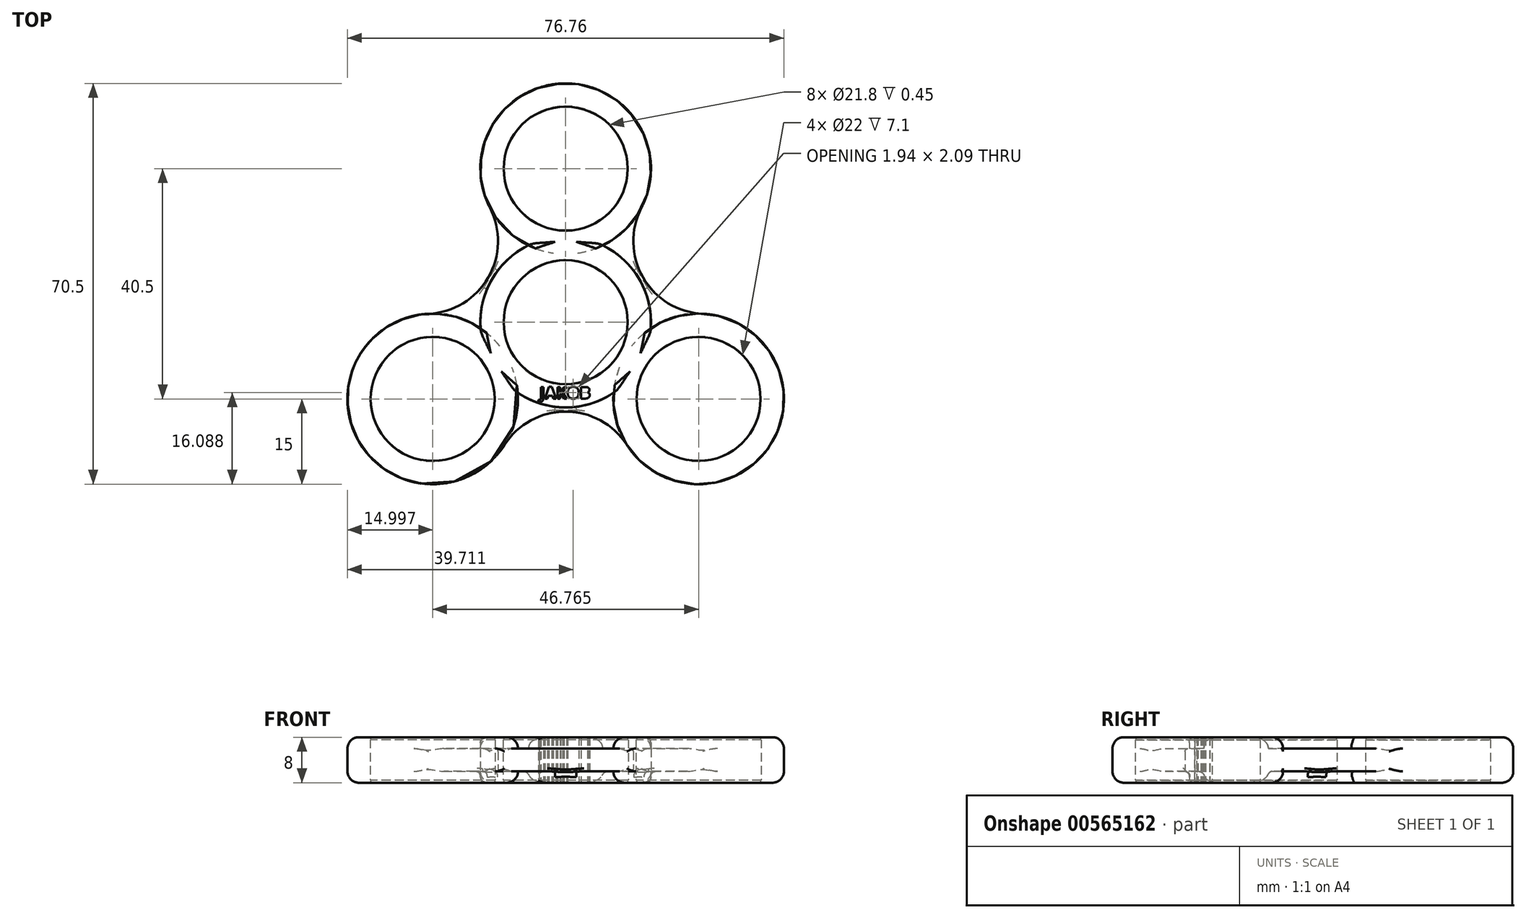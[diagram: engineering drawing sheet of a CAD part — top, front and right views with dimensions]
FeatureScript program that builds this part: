
annotation { "Feature Type Name" : "Feature", "Feature Type Description" : "" }
export const myFeature = defineFeature(function(context is Context, id is Id, definition is map)
    precondition{}
    {
        {
            var Q0;
            Q0=qCreatedBy(makeId("Top.planeOp"),FACE);
            var sketch = newSketch(context, id + "F0", { "sketchPlane" : qUnion([Q0])});
            skCircle(sketch, "E0", {"center": v(0, 0) * mm, "radius": 10.9 * mm});
            skCircle(sketch, "E1", {"center": v(0, 27) * mm, "radius": 10.9 * mm});
            skCircle(sketch, "E2.1.0", {"center": v(-23.38, -13.5) * mm, "radius": 10.9 * mm});
            skCircle(sketch, "E2.2.0", {"center": v(23.38, -13.5) * mm, "radius": 10.9 * mm});
            skArc(sketch, "E3", {"start": v(6.54, 13.5) * mm, "mid": v(0, 42) * mm, "end": v(-6.54, 13.5) * mm});
            skArc(sketch, "E4.1.0", {"start": v(8.42, -12.41) * mm, "mid": v(36.37, -21) * mm, "end": v(14.96, -1.09) * mm});
            skArc(sketch, "E4.2.0", {"start": v(-14.96, -1.09) * mm, "mid": v(-36.37, -21) * mm, "end": v(-8.42, -12.41) * mm});
            skArc(sketch, "E5", {"start": v(-8.42, -12.41) * mm, "mid": v(0, -15) * mm, "end": v(8.42, -12.41) * mm});
            skArc(sketch, "E6", {"start": v(-24.08, 1.48) * mm, "mid": v(-13.61, 7.86) * mm, "end": v(-13.33, 20.12) * mm});
            skArc(sketch, "E7", {"start": v(10.76, -21.6) * mm, "mid": v(0, -15.72) * mm, "end": v(-10.76, -21.6) * mm});
            skArc(sketch, "E8", {"start": v(13.33, 20.12) * mm, "mid": v(13.61, 7.86) * mm, "end": v(24.08, 1.48) * mm});
            skPoint(sketch, "E9.orphan", {"position": v(-13, 34.5) * mm});
            skPoint(sketch, "E10.orphan", {"position": v(-36.37, -6) * mm});
            skPoint(sketch, "E11.orphan", {"position": v(13, 34.5) * mm});
            skPoint(sketch, "E12.2.0.start.orphan", {"position": v(36.37, -6) * mm});
            skPoint(sketch, "E13.orphan", {"position": v(23.38, -28.5) * mm});
            skPoint(sketch, "E12.1.0.start.orphan", {"position": v(-23.38, -28.5) * mm});
            skArc(sketch, "E14.trimOffspring", {"start": v(14.96, -1.09) * mm, "mid": v(13, 7.5) * mm, "end": v(6.54, 13.5) * mm});
            skArc(sketch, "E15.trimOffspring", {"start": v(-6.54, 13.5) * mm, "mid": v(-13, 7.5) * mm, "end": v(-14.96, -1.09) * mm});
            skText(sketch, "E16", { "text": "JAKOB", "fontName": "OpenSans-Bold.ttf"});
            skCircle(sketch, "E17", {"center": v(23.38, -13.5) * mm, "radius": 11 * mm});
            skCircle(sketch, "E18", {"center": v(-23.38, -13.5) * mm, "radius": 11 * mm});
            skCircle(sketch, "E19", {"center": v(0, 0) * mm, "radius": 11 * mm});
            skCircle(sketch, "E20", {"center": v(0, 27) * mm, "radius": 11 * mm});
            const initialGuessF0  = {"E16": [-0.0046, -0.01343, 1, 0, 0.00205]};
            skSetInitialGuess(sketch, initialGuessF0);
            skSolve(sketch);
        }
        {
            var Q0;
            Q0=makeQuery(id+"F0.imprint","IMPRINT",FACE,{"disambiguationData":[TD([[makeQuery(id+"F0.imprint","IMPRINT",EDGE,{"derivedFrom":sQuery(id+"F0.wireOp",EDGE,"E2.1.0")}),-1.0]])]});
            var Q1;
            Q1=makeQuery(id+"F0.imprint","IMPRINT",FACE,{"disambiguationData":[TD([[makeQuery(id+"F0.imprint","IMPRINT",EDGE,{"derivedFrom":sQuery(id+"F0.wireOp",EDGE,"E0")}),-1.0]])]});
            var Q2;
            Q2=makeQuery(id+"F0.imprint","IMPRINT",FACE,{"disambiguationData":[TD([[makeQuery(id+"F0.imprint","IMPRINT",EDGE,{"derivedFrom":sQuery(id+"F0.wireOp",EDGE,"E1")}),-1.0]])]});
            var Q3;
            {var subQ0=sQuery(id+"F0.wireOp",EDGE,"E3");var subQ1=sQuery(id+"F0.wireOp",EDGE,"KJlQqC9l-gusD-toYh-YzLE-zyJcLNbmcpUm");var subQ2=makeQuery(id+"F0.imprint","INTERSECT",VERTEX,{"derivedFrom":[subQ1,subQ0]});Q3=makeQuery(id+"F0.imprint","IMPRINT",FACE,{"disambiguationData":[TD([[makeQuery(id+"F0.imprint","IMPRINT",EDGE,{"disambiguationData":[TD([[subQ2,1.0]])],"derivedFrom":subQ1}),1.0]])]});}
            var Q4;
            {var subQ0=sQuery(id+"F0.wireOp",EDGE,"E3");var subQ1=sQuery(id+"F0.wireOp",EDGE,"KJlQqC9l-gusD-toYh-YzLE-zyJcLNbmcpUm");var subQ2=makeQuery(id+"F0.imprint","INTERSECT",VERTEX,{"derivedFrom":[subQ1,subQ0]});Q4=makeQuery(id+"F0.imprint","IMPRINT",FACE,{"disambiguationData":[TD([[makeQuery(id+"F0.imprint","IMPRINT",EDGE,{"disambiguationData":[TD([[subQ2,1.0]])],"derivedFrom":subQ1}),-1.0]])]});}
            var Q5;
            {var subQ0=sQuery(id+"F0.wireOp",EDGE,"E5");var subQ1=sQuery(id+"F0.wireOp",EDGE,"E4.2.0");var subQ2=makeQuery(id+"F0.imprint","INTERSECT",VERTEX,{"disambiguationData":[OD(0.0)],"derivedFrom":[subQ1,subQ0]});Q5=makeQuery(id+"F0.imprint","IMPRINT",FACE,{"disambiguationData":[TD([[makeQuery(id+"F0.imprint","IMPRINT",EDGE,{"disambiguationData":[TD([[subQ2,-1.0]])],"derivedFrom":subQ1}),1.0]])]});}
            var Q6;
            Q6=makeQuery(id+"F0.imprint","IMPRINT",FACE,{"disambiguationData":[TD([[makeQuery(id+"F0.imprint","IMPRINT",EDGE,{"derivedFrom":sQuery(id+"F0.wireOp",EDGE,"E2.2.0")}),-1.0]])]});
            var Q7;
            {var subQ0=sQuery(id+"F0.wireOp",EDGE,"E5");var subQ1=sQuery(id+"F0.wireOp",EDGE,"E4.1.0");var subQ2=makeQuery(id+"F0.imprint","INTERSECT",VERTEX,{"disambiguationData":[OD(0.0)],"derivedFrom":[subQ1,subQ0]});Q7=makeQuery(id+"F0.imprint","IMPRINT",FACE,{"disambiguationData":[TD([[makeQuery(id+"F0.imprint","IMPRINT",EDGE,{"disambiguationData":[TD([[subQ2,-1.0]])],"derivedFrom":subQ1}),1.0]])]});}
            extrude(context, id + "F1", {"entities" : qUnion([Q0, Q1, Q2, Q3, Q4, Q5, Q6, Q7]), "endBound" : BoundingType.SYMMETRIC, "depth" : 8 * mm, "offsetDistance" : 25 * mm});
        }
        {
            var Q0;
            {var subQ0=sQuery(id+"F0.wireOp",EDGE,"E7");Q0=makeQuery(id+"F0.imprint","IMPRINT",FACE,{"disambiguationData":[TD([[makeQuery(id+"F0.imprint","IMPRINT",EDGE,{"derivedFrom":subQ0}),-1.0]])]});}
            var Q1;
            {var subQ0=sQuery(id+"F0.wireOp",EDGE,"E6");Q1=makeQuery(id+"F0.imprint","IMPRINT",FACE,{"disambiguationData":[TD([[makeQuery(id+"F0.imprint","IMPRINT",EDGE,{"derivedFrom":subQ0}),-1.0]])]});}
            var Q2;
            {var subQ0=sQuery(id+"F0.wireOp",EDGE,"E8");Q2=makeQuery(id+"F0.imprint","IMPRINT",FACE,{"disambiguationData":[TD([[makeQuery(id+"F0.imprint","IMPRINT",EDGE,{"derivedFrom":subQ0}),-1.0]])]});}
            extrude(context, id + "F2", {"entities" : qUnion([Q0, Q1, Q2]), "operationType" : NewBodyOperationType.ADD, "endBound" : BoundingType.SYMMETRIC, "depth" : 4 * mm, "offsetDistance" : 25 * mm});
        }
        {
            var Q0;
            Q0=makeQuery(id+"F1.opExtrude","CAP_EDGE",EDGE,{"disambiguationData":[OSD([sQuery(id+"F0.wireOp",EDGE,"E15.trimOffspring")])],"isStart":true});
            var Q1;
            Q1=makeQuery(id+"F2.opExtrude","CAP_EDGE",EDGE,{"disambiguationData":[OSD([sQuery(id+"F0.wireOp",EDGE,"E15.trimOffspring")])],"isStart":true});
            var Q2;
            Q2=makeQuery(id+"F1.opExtrude","CAP_EDGE",EDGE,{"disambiguationData":[OSD([sQuery(id+"F0.wireOp",EDGE,"E5")])],"isStart":true});
            var Q3;
            Q3=makeQuery(id+"F2.opExtrude","CAP_EDGE",EDGE,{"disambiguationData":[OSD([sQuery(id+"F0.wireOp",EDGE,"E5")])],"isStart":true});
            var Q4;
            Q4=makeQuery(id+"F1.opExtrude","CAP_EDGE",EDGE,{"disambiguationData":[OSD([sQuery(id+"F0.wireOp",EDGE,"E14.trimOffspring")])],"isStart":true});
            var Q5;
            Q5=makeQuery(id+"F2.opExtrude","CAP_EDGE",EDGE,{"disambiguationData":[OSD([sQuery(id+"F0.wireOp",EDGE,"E14.trimOffspring")])],"isStart":true});
            fillet(context, id + "F3", {"entities" : qUnion([Q0, Q1, Q2, Q3, Q4, Q5]), "radius" : 1 * mm, "rho" : 0.5, "crossSection" : FilletCrossSection.CONIC, "allowEdgeOverflow" : false});
        }
        {
            var Q0;
            Q0=makeQuery(id+"F1.opExtrude","CAP_EDGE",EDGE,{"disambiguationData":[OSD([sQuery(id+"F0.wireOp",EDGE,"E5")])],"isStart":false});
            var Q1;
            Q1=makeQuery(id+"F2.opExtrude","CAP_EDGE",EDGE,{"disambiguationData":[OSD([sQuery(id+"F0.wireOp",EDGE,"E5")])],"isStart":false});
            var Q2;
            Q2=makeQuery(id+"F1.opExtrude","CAP_EDGE",EDGE,{"disambiguationData":[OSD([sQuery(id+"F0.wireOp",EDGE,"E14.trimOffspring")])],"isStart":false});
            var Q3;
            Q3=makeQuery(id+"F2.opExtrude","CAP_EDGE",EDGE,{"disambiguationData":[OSD([sQuery(id+"F0.wireOp",EDGE,"E14.trimOffspring")])],"isStart":false});
            var Q4;
            Q4=makeQuery(id+"F1.opExtrude","CAP_EDGE",EDGE,{"disambiguationData":[OSD([sQuery(id+"F0.wireOp",EDGE,"E15.trimOffspring")])],"isStart":false});
            var Q5;
            Q5=makeQuery(id+"F2.opExtrude","CAP_EDGE",EDGE,{"disambiguationData":[OSD([sQuery(id+"F0.wireOp",EDGE,"E15.trimOffspring")])],"isStart":false});
            fillet(context, id + "F4", {"entities" : qUnion([Q0, Q1, Q2, Q3, Q4, Q5]), "radius" : 1 * mm, "rho" : 0.5, "crossSection" : FilletCrossSection.CONIC, "allowEdgeOverflow" : false});
        }
        {
            var Q0;
            Q0=makeQuery(id+"F1.opExtrude","CAP_EDGE",EDGE,{"disambiguationData":[OSD([sQuery(id+"F0.wireOp",EDGE,"E4.1.0")])],"isStart":false});
            var Q1;
            Q1=makeQuery(id+"F1.opExtrude","CAP_EDGE",EDGE,{"disambiguationData":[OSD([sQuery(id+"F0.wireOp",EDGE,"E3")])],"isStart":false});
            var Q2;
            Q2=makeQuery(id+"F1.opExtrude","CAP_EDGE",EDGE,{"disambiguationData":[OSD([sQuery(id+"F0.wireOp",EDGE,"E4.2.0")])],"isStart":false});
            var Q3;
            Q3=makeQuery(id+"F1.opExtrude","CAP_EDGE",EDGE,{"disambiguationData":[OSD([sQuery(id+"F0.wireOp",EDGE,"E4.2.0")])],"isStart":true});
            var Q4;
            Q4=makeQuery(id+"F1.opExtrude","CAP_EDGE",EDGE,{"disambiguationData":[OSD([sQuery(id+"F0.wireOp",EDGE,"E4.1.0")])],"isStart":true});
            var Q5;
            Q5=makeQuery(id+"F1.opExtrude","CAP_EDGE",EDGE,{"disambiguationData":[OSD([sQuery(id+"F0.wireOp",EDGE,"E3")])],"isStart":true});
            fillet(context, id + "F5", {"entities" : qUnion([Q0, Q1, Q2, Q3, Q4, Q5]), "radius" : 2 * mm, "allowEdgeOverflow" : false});
        }
        {
            var Q0;
            Q0=makeQuery(id+"F2.opExtrude","SWEPT_FACE",FACE,{"disambiguationData":[OSD([sQuery(id+"F0.wireOp",EDGE,"E8")])]});
            var Q1;
            Q1=makeQuery(id+"F2.opExtrude","SWEPT_FACE",FACE,{"disambiguationData":[OSD([sQuery(id+"F0.wireOp",EDGE,"E6")])]});
            var Q2;
            Q2=makeQuery(id+"F2.opExtrude","SWEPT_FACE",FACE,{"disambiguationData":[OSD([sQuery(id+"F0.wireOp",EDGE,"E7")])]});
            fillet(context, id + "F6", {"entities" : qUnion([Q0, Q1, Q2]), "radius" : .5 * mm, "tangentPropagation" : true, "allowEdgeOverflow" : false});
        }
        {
            var Q0;
            Q0=makeQuery(id+"F0.imprint","IMPRINT",FACE,{"disambiguationData":[TD([[makeQuery(id+"F0.imprint","IMPRINT",EDGE,{"derivedFrom":sQuery(id+"F0.wireOp",EDGE,"E20")}),1.0]])]});
            var Q1;
            Q1=makeQuery(id+"F0.imprint","IMPRINT",FACE,{"disambiguationData":[TD([[makeQuery(id+"F0.imprint","IMPRINT",EDGE,{"derivedFrom":sQuery(id+"F0.wireOp",EDGE,"E19")}),1.0]])]});
            var Q2;
            Q2=makeQuery(id+"F0.imprint","IMPRINT",FACE,{"disambiguationData":[TD([[makeQuery(id+"F0.imprint","IMPRINT",EDGE,{"derivedFrom":sQuery(id+"F0.wireOp",EDGE,"E17")}),1.0]])]});
            var Q3;
            Q3=makeQuery(id+"F0.imprint","IMPRINT",FACE,{"disambiguationData":[TD([[makeQuery(id+"F0.imprint","IMPRINT",EDGE,{"derivedFrom":sQuery(id+"F0.wireOp",EDGE,"E18")}),1.0]])]});
            extrude(context, id + "F7", {"entities" : qUnion([Q0, Q1, Q2, Q3]), "endBound" : BoundingType.SYMMETRIC, "depth" : 7.1 * mm, "offsetDistance" : 25 * mm});
        }
        {
            var Q0;
            Q0=makeQuery(id+"F7.opExtrude","SWEPT_BODY",BODY,{"disambiguationData":[OSD([sQuery(id+"F0.wireOp",EDGE,"E17")])]});
            var Q1;
            Q1=makeQuery(id+"F7.opExtrude","SWEPT_BODY",BODY,{"disambiguationData":[OSD([sQuery(id+"F0.wireOp",EDGE,"E18")])]});
            var Q2;
            Q2=makeQuery(id+"F7.opExtrude","SWEPT_BODY",BODY,{"disambiguationData":[OSD([sQuery(id+"F0.wireOp",EDGE,"E19")])]});
            var Q3;
            Q3=makeQuery(id+"F7.opExtrude","SWEPT_BODY",BODY,{"disambiguationData":[OSD([sQuery(id+"F0.wireOp",EDGE,"E20")])]});
            var Q4;
            Q4=makeQuery(id+"F1.opExtrude","SWEPT_BODY",BODY,{"disambiguationData":[OSD([sQuery(id+"F0.wireOp",EDGE,"E0"),sQuery(id+"F0.wireOp",EDGE,"E1"),sQuery(id+"F0.wireOp",EDGE,"E2.1.0"),sQuery(id+"F0.wireOp",EDGE,"E2.2.0"),sQuery(id+"F0.wireOp",EDGE,"E3"),sQuery(id+"F0.wireOp",EDGE,"E4.1.0"),sQuery(id+"F0.wireOp",EDGE,"E4.2.0"),sQuery(id+"F0.wireOp",EDGE,"E5"),sQuery(id+"F0.wireOp",EDGE,"E14.trimOffspring"),sQuery(id+"F0.wireOp",EDGE,"E15.trimOffspring"),sQuery(id+"F0.wireOp",EDGE,"E16.sketch_text.stroke-7"),sQuery(id+"F0.wireOp",EDGE,"E16.sketch_text.stroke-8"),sQuery(id+"F0.wireOp",EDGE,"E16.sketch_text.stroke-9"),sQuery(id+"F0.wireOp",EDGE,"E16.sketch_text.stroke-10"),sQuery(id+"F0.wireOp",EDGE,"E16.sketch_text.stroke-11"),sQuery(id+"F0.wireOp",EDGE,"E16.sketch_text.stroke-12"),sQuery(id+"F0.wireOp",EDGE,"E16.sketch_text.stroke-13"),sQuery(id+"F0.wireOp",EDGE,"E16.sketch_text.stroke-14"),sQuery(id+"F0.wireOp",EDGE,"E16.sketch_text.stroke-15"),sQuery(id+"F0.wireOp",EDGE,"E16.sketch_text.stroke-16"),sQuery(id+"F0.wireOp",EDGE,"E16.sketch_text.stroke-17"),sQuery(id+"F0.wireOp",EDGE,"E16.sketch_text.stroke-18"),sQuery(id+"F0.wireOp",EDGE,"E16.sketch_text.stroke-19"),sQuery(id+"F0.wireOp",EDGE,"E16.sketch_text.stroke-20"),sQuery(id+"F0.wireOp",EDGE,"E16.sketch_text.stroke-21"),sQuery(id+"F0.wireOp",EDGE,"E16.sketch_text.stroke-22"),sQuery(id+"F0.wireOp",EDGE,"E16.sketch_text.stroke-23"),sQuery(id+"F0.wireOp",EDGE,"E16.sketch_text.stroke-28"),sQuery(id+"F0.wireOp",EDGE,"E16.sketch_text.stroke-29"),sQuery(id+"F0.wireOp",EDGE,"E16.sketch_text.stroke-30"),sQuery(id+"F0.wireOp",EDGE,"E16.sketch_text.stroke-31"),sQuery(id+"F0.wireOp",EDGE,"E16.sketch_text.stroke-32"),sQuery(id+"F0.wireOp",EDGE,"E16.sketch_text.stroke-33"),sQuery(id+"F0.wireOp",EDGE,"E16.sketch_text.stroke-34"),sQuery(id+"F0.wireOp",EDGE,"E16.sketch_text.stroke-35"),sQuery(id+"F0.wireOp",EDGE,"E16.sketch_text.stroke-36"),sQuery(id+"F0.wireOp",EDGE,"E16.sketch_text.stroke-37"),sQuery(id+"F0.wireOp",EDGE,"E16.sketch_text.stroke-38"),sQuery(id+"F0.wireOp",EDGE,"E16.sketch_text.stroke-39"),sQuery(id+"F0.wireOp",EDGE,"E16.sketch_text.stroke-40"),sQuery(id+"F0.wireOp",EDGE,"E16.sketch_text.stroke-41"),sQuery(id+"F0.wireOp",EDGE,"E16.sketch_text.stroke-42"),sQuery(id+"F0.wireOp",EDGE,"E16.sketch_text.stroke-43"),sQuery(id+"F0.wireOp",EDGE,"E16.sketch_text.stroke-44"),sQuery(id+"F0.wireOp",EDGE,"E16.sketch_text.stroke-45"),sQuery(id+"F0.wireOp",EDGE,"E16.sketch_text.stroke-46"),sQuery(id+"F0.wireOp",EDGE,"E16.sketch_text.stroke-47"),sQuery(id+"F0.wireOp",EDGE,"E16.sketch_text.stroke-48"),sQuery(id+"F0.wireOp",EDGE,"E16.sketch_text.stroke-49"),sQuery(id+"F0.wireOp",EDGE,"E16.sketch_text.stroke-50"),sQuery(id+"F0.wireOp",EDGE,"E16.sketch_text.stroke-51"),sQuery(id+"F0.wireOp",EDGE,"E16.sketch_text.stroke-52"),sQuery(id+"F0.wireOp",EDGE,"E16.sketch_text.stroke-53"),sQuery(id+"F0.wireOp",EDGE,"E16.sketch_text.stroke-54"),sQuery(id+"F0.wireOp",EDGE,"E16.sketch_text.stroke-55"),sQuery(id+"F0.wireOp",EDGE,"E16.sketch_text.stroke-56"),sQuery(id+"F0.wireOp",EDGE,"E16.sketch_text.stroke-57"),sQuery(id+"F0.wireOp",EDGE,"E16.sketch_text.stroke-58"),sQuery(id+"F0.wireOp",EDGE,"E16.sketch_text.stroke-59"),sQuery(id+"F0.wireOp",EDGE,"E16.sketch_text.stroke-60"),sQuery(id+"F0.wireOp",EDGE,"E16.sketch_text.stroke-74"),sQuery(id+"F0.wireOp",EDGE,"E16.sketch_text.stroke-75"),sQuery(id+"F0.wireOp",EDGE,"E16.sketch_text.stroke-76"),sQuery(id+"F0.wireOp",EDGE,"E16.sketch_text.stroke-77"),sQuery(id+"F0.wireOp",EDGE,"E16.sketch_text.stroke-78"),sQuery(id+"F0.wireOp",EDGE,"E16.sketch_text.stroke-79"),sQuery(id+"F0.wireOp",EDGE,"E16.sketch_text.stroke-80"),sQuery(id+"F0.wireOp",EDGE,"E16.sketch_text.stroke-81"),sQuery(id+"F0.wireOp",EDGE,"E16.sketch_text.stroke-86"),sQuery(id+"F0.wireOp",EDGE,"E16.sketch_text.stroke-87"),sQuery(id+"F0.wireOp",EDGE,"E16.sketch_text.stroke-88"),sQuery(id+"F0.wireOp",EDGE,"E16.sketch_text.stroke-89"),sQuery(id+"F0.wireOp",EDGE,"E16.sketch_text.stroke-90"),sQuery(id+"F0.wireOp",EDGE,"E16.sketch_text.stroke-91"),sQuery(id+"F0.wireOp",EDGE,"E16.sketch_text.stroke-92"),sQuery(id+"F0.wireOp",EDGE,"E16.sketch_text.stroke-93"),sQuery(id+"F0.wireOp",EDGE,"E16.sketch_text.stroke-94"),sQuery(id+"F0.wireOp",EDGE,"E16.sketch_text.stroke-95"),sQuery(id+"F0.wireOp",EDGE,"E16.sketch_text.stroke-96"),sQuery(id+"F0.wireOp",EDGE,"E16.sketch_text.stroke-97"),sQuery(id+"F0.wireOp",EDGE,"E16.sketch_text.stroke-98"),sQuery(id+"F0.wireOp",EDGE,"E16.sketch_text.stroke-99"),sQuery(id+"F0.wireOp",EDGE,"E16.sketch_text.stroke-100"),sQuery(id+"F0.wireOp",EDGE,"E16.sketch_text.stroke-101"),sQuery(id+"F0.wireOp",EDGE,"E16.sketch_text.stroke-102"),sQuery(id+"F0.wireOp",EDGE,"E16.sketch_text.stroke-103"),sQuery(id+"F0.wireOp",EDGE,"E16.sketch_text.stroke-104"),sQuery(id+"F0.wireOp",EDGE,"E16.sketch_text.stroke-105"),sQuery(id+"F0.wireOp",EDGE,"E16.sketch_text.stroke-106"),sQuery(id+"F0.wireOp",EDGE,"E16.sketch_text.stroke-107"),sQuery(id+"F0.wireOp",EDGE,"E16.sketch_text.stroke-108"),sQuery(id+"F0.wireOp",EDGE,"E16.sketch_text.stroke-109"),sQuery(id+"F0.wireOp",EDGE,"E16.sketch_text.stroke-110"),sQuery(id+"F0.wireOp",EDGE,"E16.sketch_text.stroke-111"),sQuery(id+"F0.wireOp",EDGE,"E16.sketch_text.stroke-112"),sQuery(id+"F0.wireOp",EDGE,"E16.sketch_text.stroke-113"),sQuery(id+"F0.wireOp",EDGE,"E16.sketch_text.stroke-114"),sQuery(id+"F0.wireOp",EDGE,"E16.sketch_text.stroke-115"),sQuery(id+"F0.wireOp",EDGE,"E16.sketch_text.stroke-116"),sQuery(id+"F0.wireOp",EDGE,"E16.sketch_text.stroke-117"),sQuery(id+"F0.wireOp",EDGE,"E16.sketch_text.stroke-118"),sQuery(id+"F0.wireOp",EDGE,"E16.sketch_text.stroke-119"),sQuery(id+"F0.wireOp",EDGE,"E16.sketch_text.stroke-120"),sQuery(id+"F0.wireOp",EDGE,"E16.sketch_text.stroke-121"),sQuery(id+"F0.wireOp",EDGE,"E16.sketch_text.stroke-122"),sQuery(id+"F0.wireOp",EDGE,"E16.sketch_text.stroke-123"),sQuery(id+"F0.wireOp",EDGE,"E16.sketch_text.stroke-124"),sQuery(id+"F0.wireOp",EDGE,"E16.sketch_text.stroke-125"),sQuery(id+"F0.wireOp",EDGE,"E16.sketch_text.stroke-126"),sQuery(id+"F0.wireOp",EDGE,"E16.sketch_text.stroke-127"),sQuery(id+"F0.wireOp",EDGE,"E16.sketch_text.stroke-128"),sQuery(id+"F0.wireOp",EDGE,"E16.sketch_text.stroke-129"),sQuery(id+"F0.wireOp",EDGE,"E16.sketch_text.stroke-130"),sQuery(id+"F0.wireOp",EDGE,"E16.sketch_text.stroke-131"),sQuery(id+"F0.wireOp",EDGE,"E16.sketch_text.stroke-132"),sQuery(id+"F0.wireOp",EDGE,"E16.sketch_text.stroke-133"),sQuery(id+"F0.wireOp",EDGE,"E16.sketch_text.stroke-134"),sQuery(id+"F0.wireOp",EDGE,"E16.sketch_text.stroke-135"),sQuery(id+"F0.wireOp",EDGE,"E16.sketch_text.stroke-136"),sQuery(id+"F0.wireOp",EDGE,"E16.sketch_text.stroke-137"),sQuery(id+"F0.wireOp",EDGE,"E16.sketch_text.stroke-138"),sQuery(id+"F0.wireOp",EDGE,"E16.sketch_text.stroke-139"),sQuery(id+"F0.wireOp",EDGE,"E16.sketch_text.stroke-140"),sQuery(id+"F0.wireOp",EDGE,"E16.sketch_text.stroke-141"),sQuery(id+"F0.wireOp",EDGE,"E16.sketch_text.stroke-142"),sQuery(id+"F0.wireOp",EDGE,"E16.sketch_text.stroke-143"),sQuery(id+"F0.wireOp",EDGE,"E16.sketch_text.stroke-144"),sQuery(id+"F0.wireOp",EDGE,"E16.sketch_text.stroke-145"),sQuery(id+"F0.wireOp",EDGE,"E16.sketch_text.stroke-146"),sQuery(id+"F0.wireOp",EDGE,"E16.sketch_text.stroke-147"),sQuery(id+"F0.wireOp",EDGE,"E16.sketch_text.stroke-148"),sQuery(id+"F0.wireOp",EDGE,"E16.sketch_text.stroke-149"),sQuery(id+"F0.wireOp",EDGE,"E16.sketch_text.stroke-150"),sQuery(id+"F0.wireOp",EDGE,"E16.sketch_text.stroke-151"),sQuery(id+"F0.wireOp",EDGE,"E16.sketch_text.stroke-152"),sQuery(id+"F0.wireOp",EDGE,"E16.sketch_text.stroke-153"),sQuery(id+"F0.wireOp",EDGE,"E16.sketch_text.stroke-154"),sQuery(id+"F0.wireOp",EDGE,"E16.sketch_text.stroke-155"),sQuery(id+"F0.wireOp",EDGE,"E16.sketch_text.stroke-156"),sQuery(id+"F0.wireOp",EDGE,"E16.sketch_text.stroke-157"),sQuery(id+"F0.wireOp",EDGE,"E16.sketch_text.stroke-158"),sQuery(id+"F0.wireOp",EDGE,"E16.sketch_text.stroke-159"),sQuery(id+"F0.wireOp",EDGE,"E16.sketch_text.stroke-160"),sQuery(id+"F0.wireOp",EDGE,"E16.sketch_text.stroke-161"),sQuery(id+"F0.wireOp",EDGE,"E16.sketch_text.stroke-162"),sQuery(id+"F0.wireOp",EDGE,"E16.sketch_text.stroke-163"),sQuery(id+"F0.wireOp",EDGE,"E16.sketch_text.stroke-164"),sQuery(id+"F0.wireOp",EDGE,"E16.sketch_text.stroke-165"),sQuery(id+"F0.wireOp",EDGE,"E16.sketch_text.stroke-166"),sQuery(id+"F0.wireOp",EDGE,"E16.sketch_text.stroke-167"),sQuery(id+"F0.wireOp",EDGE,"E16.sketch_text.stroke-168"),sQuery(id+"F0.wireOp",EDGE,"E16.sketch_text.stroke-169"),sQuery(id+"F0.wireOp",EDGE,"E16.sketch_text.stroke-170")])]});
            booleanBodies(context, id + "F8", {"operationType" : BooleanOperationType.SUBTRACTION, "tools" : qUnion([Q0, Q1, Q2, Q3]), "targets" : qUnion([Q4])});
        }
    });
